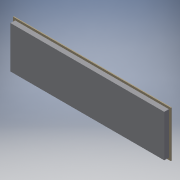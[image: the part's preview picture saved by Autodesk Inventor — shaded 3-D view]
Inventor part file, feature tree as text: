
AUTODESK INVENTOR PART (.ipt)
format: ipt  version: 2019 (Build 230136000, 136)  size: 100,864 bytes
history: native  units: mm
features: other x6, reference x4, extrude x2, sketch x2
ambient origin geometry x8: Origin, YZ Plane, XZ Plane, XY Plane, X Axis, Y Axis, Z Axis, Center Point
bodies: Solid1 (feature_tree)
feature tree (14):
  extrude  "Extrusion1"  Depth=861.06mm
  extrude  "Extrusion2"  Depth=25.4mm TaperAngle=0.0deg
  sketch  "Sketch1"  dims[d0=4.7625mm d1=0.0mm d2=861.06mm]
  sketch  "Sketch2"  dims[d3=251.46mm d4=25.4mm d5=0.0mm]
  reference  "Reference1"
  reference  "Reference2"
  reference  "Reference3"
  reference  "Reference4"
  parser-record x1  (decoder bookkeeping rows leaked as tree rows — omitted from the tree; the rows remain in map.json)
  other  "enclosure.iam"
  other  "1515-S-BLACK_rear_top_cross:1"
  other  "1515-S-BLACK_side_short_top:1"
  other  "1515-S-BLACK_top_hatch_cross:1"
  other  "1515-S-BLACK_side_short_top:2"
note: 1 file-system path scrubbed to <path> (originals preserved in map.json)
